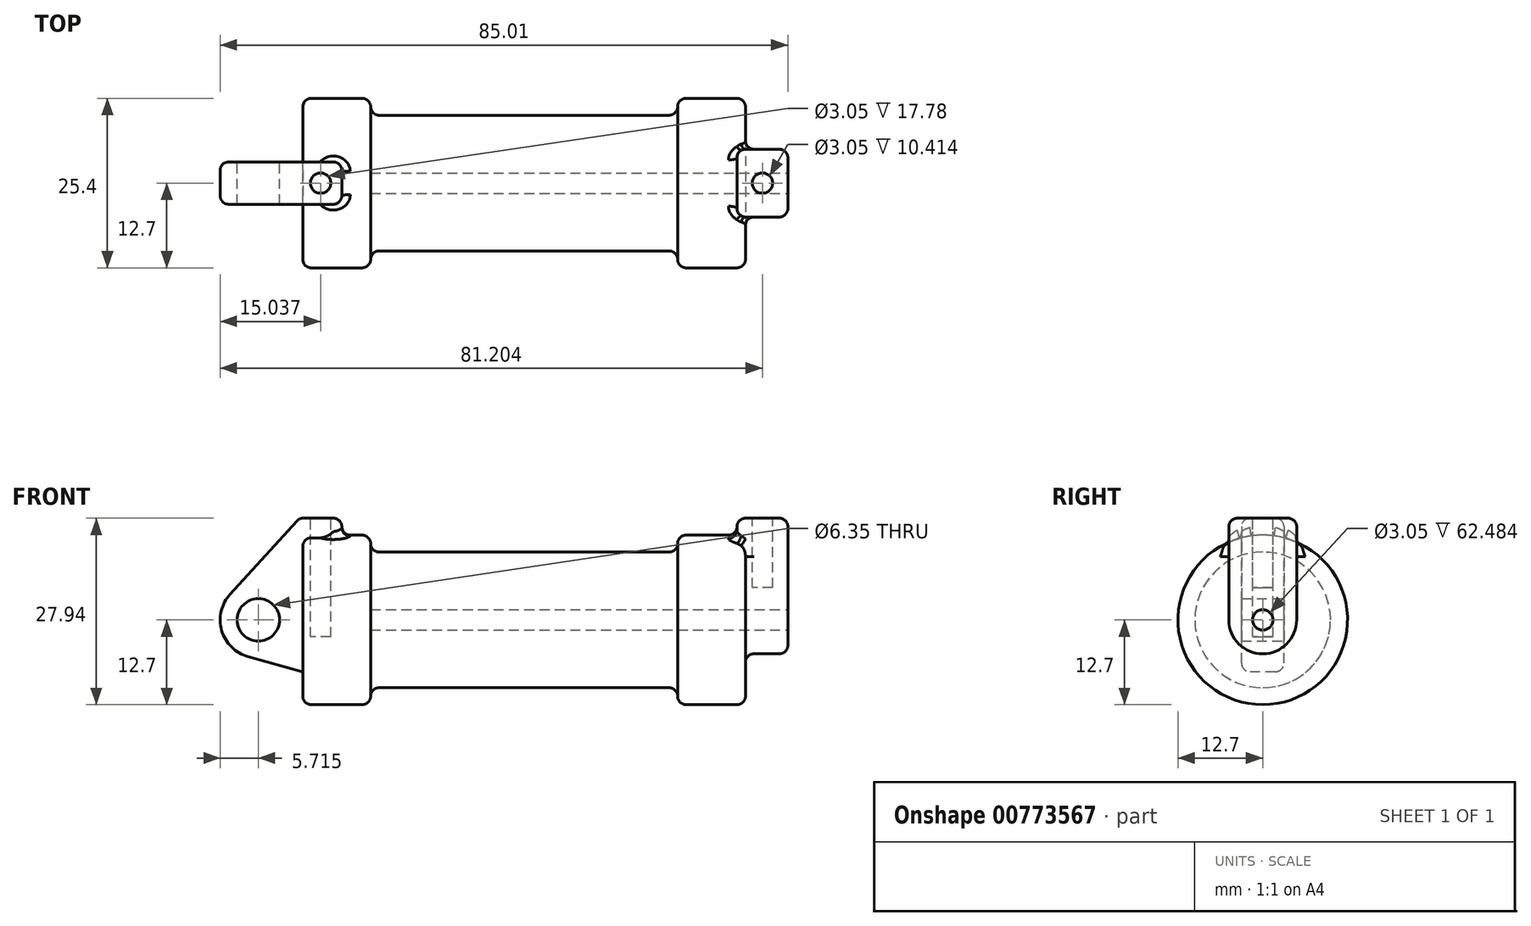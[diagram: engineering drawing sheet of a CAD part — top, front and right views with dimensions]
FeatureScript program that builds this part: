
annotation { "Feature Type Name" : "Feature", "Feature Type Description" : "" }
export const myFeature = defineFeature(function(context is Context, id is Id, definition is map)
    precondition{}
    {
        {
            var Q0;
            Q0=qCreatedBy(makeId("Front.planeOp"),FACE);
            var sketch = newSketch(context, id + "F0", { "sketchPlane" : qUnion([Q0])});
            skLineSegment(sketch, "E0", {"start": v(0, 0) * mm, "end": v(0, 12.7) * mm});
            skLineSegment(sketch, "E1", {"start": v(0, 12.7) * mm, "end": v(10.16, 12.7) * mm});
            skLineSegment(sketch, "E2", {"start": v(10.16, 12.7) * mm, "end": v(10.16, 10.16) * mm});
            skLineSegment(sketch, "E3", {"start": v(10.16, 10.16) * mm, "end": v(56.13, 10.16) * mm});
            skLineSegment(sketch, "E4", {"start": v(56.13, 10.16) * mm, "end": v(56.13, 12.7) * mm});
            skLineSegment(sketch, "E5", {"start": v(56.13, 12.7) * mm, "end": v(66.3, 12.7) * mm});
            skLineSegment(sketch, "E6", {"start": v(66.3, 12.7) * mm, "end": v(66.3, 0) * mm});
            skLineSegment(sketch, "E7", {"start": v(66.3, 0) * mm, "end": v(0, 0) * mm});
            skLineSegment(sketch, "E8", {"start": v(5.84, 15.24) * mm, "end": v(-0.5, 15.24) * mm});
            skLineSegment(sketch, "E9", {"start": v(-0.5, 15.24) * mm, "end": v(-10.88, 3.85) * mm});
            skLineSegment(sketch, "E10", {"start": v(0, 0) * mm, "end": v(-6.65, 0) * mm});
            skCircle(sketch, "E11", {"center": v(-6.65, 0) * mm, "radius": 5.72 * mm});
            skCircle(sketch, "E12", {"center": v(-6.65, 0) * mm, "radius": 3.18 * mm});
            skLineSegment(sketch, "E13", {"start": v(5.84, 15.24) * mm, "end": v(5.84, -9.4) * mm});
            skLineSegment(sketch, "E14", {"start": v(5.84, -9.4) * mm, "end": v(-8.18, -5.5) * mm});
            skSolve(sketch);
        }
        {
            var Q0;
            {var subQ0=sQuery(id+"F0.wireOp",EDGE,"E0");Q0=makeQuery(id+"F0.imprint","IMPRINT",FACE,{"disambiguationData":[TD([[makeQuery(id+"F0.imprint","IMPRINT",EDGE,{"derivedFrom":subQ0}),-1.0]])]});}
            var Q1;
            {var subQ0=sQuery(id+"F0.wireOp",EDGE,"E2");Q1=makeQuery(id+"F0.imprint","IMPRINT",FACE,{"disambiguationData":[TD([[makeQuery(id+"F0.imprint","IMPRINT",EDGE,{"derivedFrom":subQ0}),-1.0]])]});}
            var Q2;
            Q2=sQuery(id+"F0.wireOp",EDGE,"E7");
            revolve(context, id + "F1", {"surfaceOperationType" : NewSurfaceOperationType.NEW, "entities" : qUnion([Q0, Q1]), "axis" : qUnion([Q2]), "revolveType" : RevolveType.FULL});
        }
        {
            var Q0;
            {var subQ1=sQuery(id+"F0.wireOp",EDGE,"E0");Q0=makeQuery(id+"F0.imprint","IMPRINT",FACE,{"disambiguationData":[TD([[makeQuery(id+"F0.imprint","IMPRINT",EDGE,{"derivedFrom":subQ1}),1.0]])]});}
            var Q1;
            {var subQ5=sQuery(id+"F0.wireOp",EDGE,"E12");Q1=makeQuery(id+"F0.imprint","IMPRINT",FACE,{"disambiguationData":[TD([[makeQuery(id+"F0.imprint","IMPRINT",EDGE,{"derivedFrom":subQ5}),-1.0]])]});}
            var Q2;
            {var subQ0=sQuery(id+"F0.wireOp",EDGE,"E14");Q2=makeQuery(id+"F0.imprint","IMPRINT",FACE,{"disambiguationData":[TD([[makeQuery(id+"F0.imprint","IMPRINT",EDGE,{"derivedFrom":subQ0}),-1.0]])]});}
            var Q3;
            {var subQ0=sQuery(id+"F0.wireOp",EDGE,"E0");Q3=makeQuery(id+"F0.imprint","IMPRINT",FACE,{"disambiguationData":[TD([[makeQuery(id+"F0.imprint","IMPRINT",EDGE,{"derivedFrom":subQ0}),-1.0]])]});}
            var Q4;
            Q4=sQuery(id+"F0.wireOp",EDGE,"E9");
            var Q5;
            Q5=sQuery(id+"F0.wireOp",EDGE,"E8");
            var Q6;
            Q6=sQuery(id+"F0.wireOp",EDGE,"E13");
            var Q7;
            Q7=sQuery(id+"F0.wireOp",EDGE,"E14");
            var Q8;
            Q8=sQuery(id+"F0.wireOp",EDGE,"E11");
            var Q9;
            Q9=sQuery(id+"F0.wireOp",EDGE,"E12");
            extrude(context, id + "F2", {"entities" : qUnion([Q0, Q1, Q2, Q3]), "surfaceEntities" : qUnion([Q4, Q5, Q6, Q7, Q8, Q9]), "endBound" : BoundingType.SYMMETRIC, "depth" : 6.35 * mm, "offsetDistance" : 25.4 * mm});
        }
        {
            var Q0;
            Q0=makeQuery(id+"F1.opRevolve","SWEPT_FACE",FACE,{"disambiguationData":[OSD([sQuery(id+"F0.wireOp",EDGE,"E6")])]});
            var sketch = newSketch(context, id + "F3", { "sketchPlane" : qUnion([Q0])});
            skCircle(sketch, "E15", {"center": v(0, 0) * mm, "radius": 1.52 * mm});
            skCircle(sketch, "E16", {"center": v(0, 0) * mm, "radius": 5.08 * mm});
            skLineSegment(sketch, "E17", {"start": v(-5.08, 0) * mm, "end": v(-5.08, 15.24) * mm});
            skLineSegment(sketch, "E18", {"start": v(5.08, 0) * mm, "end": v(5.08, 15.24) * mm});
            skLineSegment(sketch, "E19", {"start": v(-5.08, 15.24) * mm, "end": v(5.08, 15.24) * mm});
            skSolve(sketch);
        }
        {
            var Q0;
            {var subQ0=sQuery(id+"F3.wireOp",EDGE,"E17");var subQ1=sQuery(id+"F3.wireOp",EDGE,"E16");var subQ2=makeQuery(id+"F3.imprint","INTERSECT",VERTEX,{"derivedFrom":[subQ1,subQ0]});Q0=makeQuery(id+"F3.imprint","IMPRINT",FACE,{"disambiguationData":[TD([[makeQuery(id+"F3.imprint","IMPRINT",EDGE,{"disambiguationData":[TD([[subQ2,1.0]])],"derivedFrom":subQ1}),-1.0]])]});}
            var Q1;
            {var subQ0=sQuery(id+"F3.wireOp",EDGE,"E19");Q1=makeQuery(id+"F3.imprint","IMPRINT",FACE,{"disambiguationData":[TD([[makeQuery(id+"F3.imprint","IMPRINT",EDGE,{"derivedFrom":subQ0}),-1.0]])]});}
            var Q2;
            Q2=makeQuery(id+"F3.imprint","IMPRINT",FACE,{"disambiguationData":[TD([[makeQuery(id+"F3.imprint","IMPRINT",EDGE,{"derivedFrom":sQuery(id+"F3.wireOp",EDGE,"E15")}),-1.0]])]});
            extrude(context, id + "F4", {"entities" : qUnion([Q0, Q1, Q2]), "operationType" : NewBodyOperationType.ADD, "oppositeDirection" : true, "depth" : 1.27 * mm, "offsetDistance" : 25.4 * mm, "hasSecondDirection" : true, "secondDirectionOppositeDirection" : false, "secondDirectionDepth" : 6.35 * mm});
        }
        {
            var Q0;
            Q0=makeQuery(id+"F4.boolean.opBoolean","SPLIT",FACE,{"disambiguationData":[TD([makeQuery(id+"F4.opExtrude","SWEPT_FACE",FACE,{"disambiguationData":[OSD([sQuery(id+"F3.wireOp",EDGE,"E15")])]})])],"derivedFrom":makeQuery(id+"F1.opRevolve","SWEPT_FACE",FACE,{"disambiguationData":[OSD([sQuery(id+"F0.wireOp",EDGE,"E6")])]})});
            var Q1;
            Q1=makeQuery(id+"F1.opRevolve","SWEPT_FACE",FACE,{"disambiguationData":[OSD([sQuery(id+"F0.wireOp",EDGE,"E2")])]});
            extrude(context, id + "F5", {"entities" : qUnion([Q0]), "operationType" : NewBodyOperationType.REMOVE, "endBound" : BoundingType.UP_TO_SURFACE, "oppositeDirection" : true, "depth" : 25.4 * mm, "endBoundEntityFace" : qUnion([Q1]), "offsetDistance" : 25.4 * mm});
        }
        {
            var Q0;
            Q0=makeQuery(id+"F4.opExtrude","SWEPT_FACE",FACE,{"disambiguationData":[OSD([sQuery(id+"F3.wireOp",EDGE,"E19")])]});
            var sketch = newSketch(context, id + "F6", { "sketchPlane" : qUnion([Q0])});
            skLineSegment(sketch, "E20.0", {"start": v(5.84, -3.18) * mm, "end": v(-0.5, -3.18) * mm, "construction": true});
            skLineSegment(sketch, "E20.1", {"start": v(-0.5, -3.18) * mm, "end": v(-0.5, 3.17) * mm, "construction": true});
            skLineSegment(sketch, "E20.2", {"start": v(5.84, 3.18) * mm, "end": v(-0.5, 3.18) * mm, "construction": true});
            skLineSegment(sketch, "E20.3", {"start": v(5.84, -3.18) * mm, "end": v(5.84, 3.17) * mm, "construction": true});
            skLineSegment(sketch, "E20.4", {"start": v(65.02, -5.08) * mm, "end": v(65.02, 5.08) * mm, "construction": true});
            skLineSegment(sketch, "E20.5", {"start": v(65.02, 5.08) * mm, "end": v(72.64, 5.08) * mm, "construction": true});
            skLineSegment(sketch, "E20.6", {"start": v(72.64, -5.08) * mm, "end": v(72.64, 5.08) * mm, "construction": true});
            skLineSegment(sketch, "E20.7", {"start": v(65.02, -5.08) * mm, "end": v(72.64, -5.08) * mm, "construction": true});
            skLineSegment(sketch, "E21", {"start": v(72.64, -5.08) * mm, "end": v(65.02, 5.08) * mm, "construction": true});
            skCircle(sketch, "E22", {"center": v(68.83, 0) * mm, "radius": 1.52 * mm});
            skLineSegment(sketch, "E23", {"start": v(5.84, -3.18) * mm, "end": v(-0.5, 3.17) * mm, "construction": true});
            skCircle(sketch, "E24", {"center": v(2.67, 0) * mm, "radius": 1.52 * mm});
            skSolve(sketch);
        }
        {
            var Q0;
            Q0=makeQuery(id+"F6.imprint","IMPRINT",FACE,{"disambiguationData":[TD([[makeQuery(id+"F6.imprint","IMPRINT",EDGE,{"derivedFrom":sQuery(id+"F6.wireOp",EDGE,"E24")}),1.0]])]});
            var Q1;
            Q1=sQuery(id+"F6.wireOp",EDGE,"E24");
            extrude(context, id + "F7", {"entities" : qUnion([Q0]), "operationType" : NewBodyOperationType.REMOVE, "surfaceEntities" : qUnion([Q1]), "oppositeDirection" : true, "depth" : 17.78 * mm, "offsetDistance" : 25.4 * mm});
        }
        {
            var Q0;
            Q0=makeQuery(id+"F2.opExtrude","SWEPT_BODY",BODY,{"disambiguationData":[OSD([sQuery(id+"F0.wireOp",EDGE,"E8"),sQuery(id+"F0.wireOp",EDGE,"E9"),sQuery(id+"F0.wireOp",EDGE,"E11"),sQuery(id+"F0.wireOp",EDGE,"E12"),sQuery(id+"F0.wireOp",EDGE,"E13"),sQuery(id+"F0.wireOp",EDGE,"E14")])]});
            var Q1;
            Q1=makeQuery(id+"F1.opRevolve","SWEPT_BODY",BODY,{"disambiguationData":[OSD([sQuery(id+"F0.wireOp",EDGE,"E0"),sQuery(id+"F0.wireOp",EDGE,"E1"),sQuery(id+"F0.wireOp",EDGE,"E2"),sQuery(id+"F0.wireOp",EDGE,"E3"),sQuery(id+"F0.wireOp",EDGE,"E4"),sQuery(id+"F0.wireOp",EDGE,"E5"),sQuery(id+"F0.wireOp",EDGE,"E6"),sQuery(id+"F0.wireOp",EDGE,"E7")])]});
            booleanBodies(context, id + "F8", {"operationType" : BooleanOperationType.UNION, "tools" : qUnion([Q0, Q1])});
        }
        {
            var Q0;
            Q0=makeQuery(id+"F6.imprint","IMPRINT",FACE,{"disambiguationData":[TD([[makeQuery(id+"F6.imprint","IMPRINT",EDGE,{"derivedFrom":sQuery(id+"F6.wireOp",EDGE,"E22")}),1.0]])]});
            var Q1;
            Q1=sQuery(id+"F6.wireOp",EDGE,"E22");
            extrude(context, id + "F9", {"entities" : qUnion([Q0]), "operationType" : NewBodyOperationType.REMOVE, "surfaceEntities" : qUnion([Q1]), "oppositeDirection" : true, "depth" : 10.4 * mm, "offsetDistance" : 25.4 * mm});
        }
        {
            var Q0;
            Q0=makeQuery(id+"F1.opRevolve","SWEPT_EDGE",EDGE,{"disambiguationData":[OSD([sQuery(id+"F0.wireOp",EDGE,"E5"),sQuery(id+"F0.wireOp",EDGE,"E6")])]});
            var Q1;
            Q1=makeQuery(id+"F1.opRevolve","SWEPT_EDGE",EDGE,{"disambiguationData":[OSD([sQuery(id+"F0.wireOp",EDGE,"E4"),sQuery(id+"F0.wireOp",EDGE,"E5")])]});
            var Q2;
            Q2=makeQuery(id+"F1.opRevolve","SWEPT_EDGE",EDGE,{"disambiguationData":[OSD([sQuery(id+"F0.wireOp",EDGE,"E3"),sQuery(id+"F0.wireOp",EDGE,"E4")])]});
            var Q3;
            Q3=makeQuery(id+"F1.opRevolve","SWEPT_EDGE",EDGE,{"disambiguationData":[OSD([sQuery(id+"F0.wireOp",EDGE,"E2"),sQuery(id+"F0.wireOp",EDGE,"E3")])]});
            var Q4;
            Q4=makeQuery(id+"F1.opRevolve","SWEPT_EDGE",EDGE,{"disambiguationData":[OSD([sQuery(id+"F0.wireOp",EDGE,"E1"),sQuery(id+"F0.wireOp",EDGE,"E2")])]});
            var Q5;
            Q5=makeQuery(id+"F1.opRevolve","SWEPT_EDGE",EDGE,{"disambiguationData":[OSD([sQuery(id+"F0.wireOp",EDGE,"E0"),sQuery(id+"F0.wireOp",EDGE,"E1")])]});
            fillet(context, id + "F10", {"entities" : qUnion([Q0, Q1, Q2, Q3, Q4, Q5]), "radius" : 1.27 * mm, "tangentPropagation" : true, "allowEdgeOverflow" : false});
        }
        {
            var Q0;
            Q0=makeQuery(id+"F4.opExtrude","CAP_EDGE",EDGE,{"disambiguationData":[OSD([sQuery(id+"F3.wireOp",EDGE,"E17")])],"isStart":false});
            var Q1;
            Q1=makeQuery(id+"F4.opExtrude","SWEPT_EDGE",EDGE,{"disambiguationData":[OSD([sQuery(id+"F3.wireOp",EDGE,"E17"),sQuery(id+"F3.wireOp",EDGE,"E19")])]});
            var Q2;
            Q2=makeQuery(id+"F4.opExtrude","CAP_EDGE",EDGE,{"disambiguationData":[OSD([sQuery(id+"F3.wireOp",EDGE,"E19")])],"isStart":false});
            var Q3;
            Q3=makeQuery(id+"F4.opExtrude","CAP_EDGE",EDGE,{"disambiguationData":[OSD([sQuery(id+"F3.wireOp",EDGE,"E19")])],"isStart":true});
            var Q4;
            Q4=makeQuery(id+"F4.opExtrude","SWEPT_EDGE",EDGE,{"disambiguationData":[OSD([sQuery(id+"F3.wireOp",EDGE,"E18"),sQuery(id+"F3.wireOp",EDGE,"E19")])]});
            var Q5;
            Q5=makeQuery(id+"F4.opExtrude","CAP_EDGE",EDGE,{"disambiguationData":[OSD([sQuery(id+"F3.wireOp",EDGE,"E17")])],"isStart":true});
            var Q6;
            Q6=makeQuery(id+"F4.opExtrude","CAP_EDGE",EDGE,{"disambiguationData":[OSD([sQuery(id+"F3.wireOp",EDGE,"E18")])],"isStart":false});
            var Q7;
            Q7=makeQuery(id+"F4.opExtrude","CAP_EDGE",EDGE,{"disambiguationData":[OSD([sQuery(id+"F3.wireOp",EDGE,"E18")])],"isStart":true});
            fillet(context, id + "F11", {"entities" : qUnion([Q0, Q1, Q2, Q3, Q4, Q5, Q6, Q7]), "radius" : 1.27 * mm, "tangentPropagation" : true, "allowEdgeOverflow" : false});
        }
        {
            var Q0;
            Q0=makeQuery(id+"F4.boolean.opBoolean","INTERSECT",EDGE,{"derivedFrom":[makeQuery(id+"F1.opRevolve","SWEPT_FACE",FACE,{"disambiguationData":[OSD([sQuery(id+"F0.wireOp",EDGE,"E5")])]}),makeQuery(id+"F4.opExtrude","CAP_FACE",FACE,{"disambiguationData":[OSD([sQuery(id+"F3.wireOp",EDGE,"E15"),sQuery(id+"F3.wireOp",EDGE,"E16"),sQuery(id+"F3.wireOp",EDGE,"E17"),sQuery(id+"F3.wireOp",EDGE,"E18"),sQuery(id+"F3.wireOp",EDGE,"E19")])],"isStart":false})]});
            fillet(context, id + "F12", {"entities" : qUnion([Q0]), "radius" : 1.27 * mm, "tangentPropagation" : true, "allowEdgeOverflow" : false});
        }
        {
            var Q0;
            Q0=makeQuery(id+"F2.opExtrude","CAP_EDGE",EDGE,{"disambiguationData":[OSD([sQuery(id+"F0.wireOp",EDGE,"E9")])],"isStart":false});
            var Q1;
            Q1=makeQuery(id+"F2.opExtrude","CAP_EDGE",EDGE,{"disambiguationData":[OSD([sQuery(id+"F0.wireOp",EDGE,"E9")])],"isStart":true});
            var Q2;
            Q2=makeQuery(id+"F2.opExtrude","CAP_EDGE",EDGE,{"disambiguationData":[OSD([sQuery(id+"F0.wireOp",EDGE,"E8")])],"isStart":true});
            var Q3;
            Q3=makeQuery(id+"F2.opExtrude","CAP_EDGE",EDGE,{"disambiguationData":[OSD([sQuery(id+"F0.wireOp",EDGE,"E8")])],"isStart":false});
            var Q4;
            Q4=makeQuery(id+"F2.opExtrude","SWEPT_EDGE",EDGE,{"disambiguationData":[OSD([sQuery(id+"F0.wireOp",EDGE,"E8"),sQuery(id+"F0.wireOp",EDGE,"E9")])]});
            var Q5;
            Q5=makeQuery(id+"F2.opExtrude","SWEPT_EDGE",EDGE,{"disambiguationData":[OSD([sQuery(id+"F0.wireOp",EDGE,"E8"),sQuery(id+"F0.wireOp",EDGE,"E13")])]});
            var Q6;
            Q6=makeQuery(id+"F2.opExtrude","CAP_EDGE",EDGE,{"disambiguationData":[OSD([sQuery(id+"F0.wireOp",EDGE,"E13")])],"isStart":false});
            var Q7;
            Q7=makeQuery(id+"F2.opExtrude","CAP_EDGE",EDGE,{"disambiguationData":[OSD([sQuery(id+"F0.wireOp",EDGE,"E13")])],"isStart":true});
            var Q8;
            Q8=makeQuery(id+"F8.opBoolean","INTERSECT",EDGE,{"derivedFrom":[makeQuery(id+"F2.opExtrude","SWEPT_FACE",FACE,{"disambiguationData":[OSD([sQuery(id+"F0.wireOp",EDGE,"E13")])]}),makeQuery(id+"F1.opRevolve","SWEPT_FACE",FACE,{"disambiguationData":[OSD([sQuery(id+"F0.wireOp",EDGE,"E1")])]})]});
            fillet(context, id + "F13", {"entities" : qUnion([Q0, Q1, Q2, Q3, Q4, Q5, Q6, Q7, Q8]), "radius" : 1.27 * mm, "tangentPropagation" : true, "allowEdgeOverflow" : false});
        }
    });
